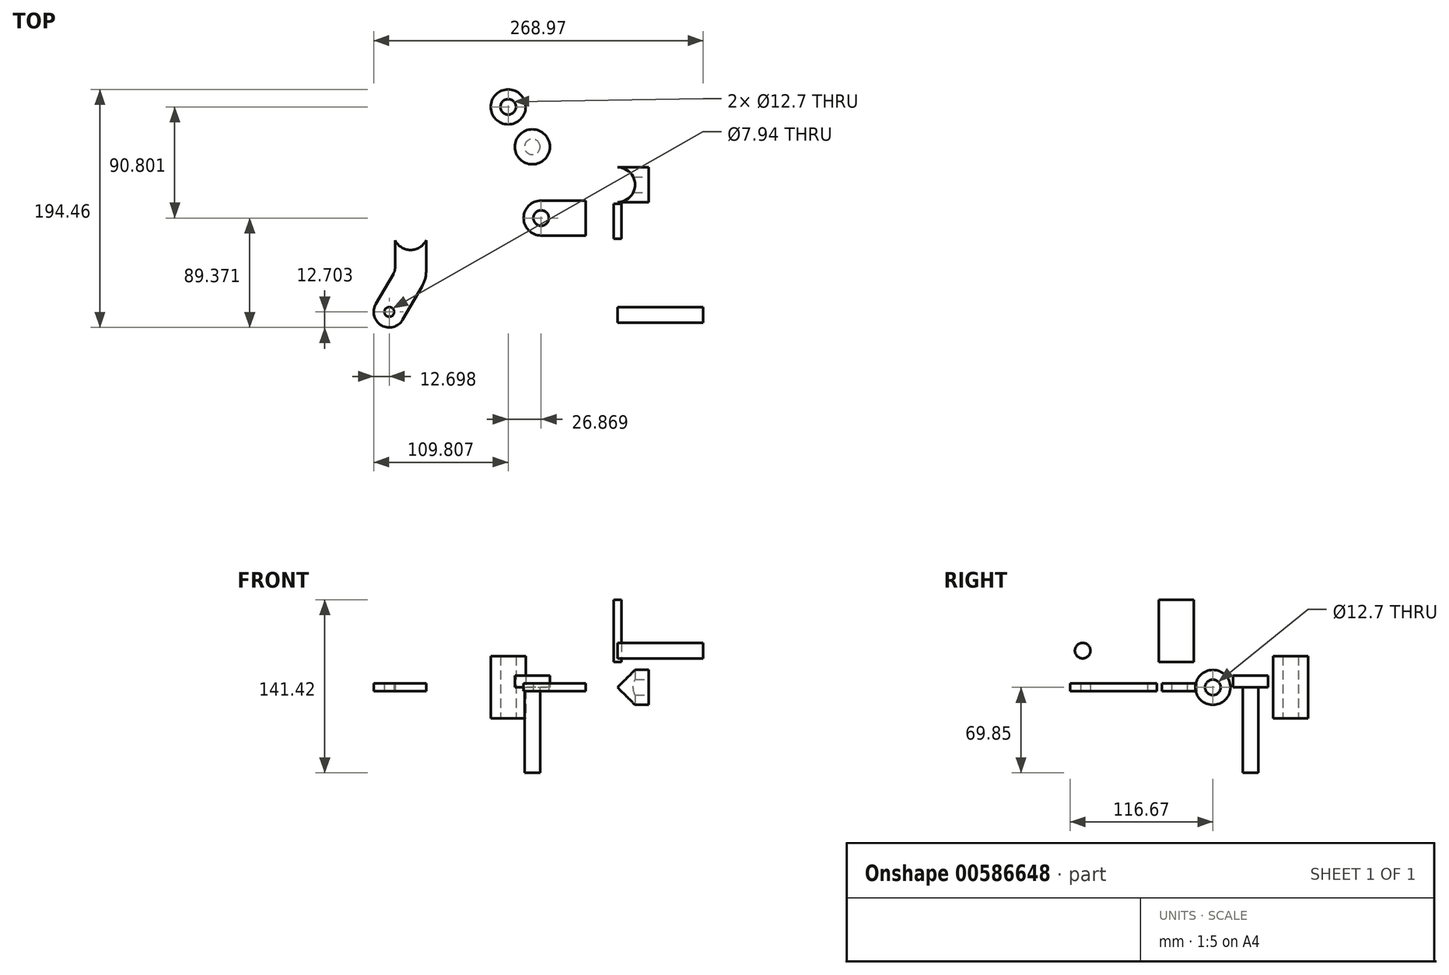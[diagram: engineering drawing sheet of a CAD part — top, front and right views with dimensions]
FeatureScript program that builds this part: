
annotation { "Feature Type Name" : "Feature", "Feature Type Description" : "" }
export const myFeature = defineFeature(function(context is Context, id is Id, definition is map)
    precondition{}
    {
        {
            var Q0;
            Q0=qCreatedBy(makeId("Top.planeOp"),FACE);
            var sketch = newSketch(context, id + "F0", { "sketchPlane" : qUnion([Q0])});
            skLineSegment(sketch, "E0.bottom", {"start": v(-76.73, -13.01) * mm, "end": v(-25.93, -13.01) * mm});
            skLineSegment(sketch, "E0.top", {"start": v(-76.73, -41.59) * mm, "end": v(-25.93, -41.59) * mm});
            skLineSegment(sketch, "E0.left", {"start": v(-76.73, -13.01) * mm, "end": v(-76.73, -41.59) * mm});
            skLineSegment(sketch, "E0.right", {"start": v(-25.93, -13.01) * mm, "end": v(-25.93, -41.59) * mm});
            skCircle(sketch, "E1", {"center": v(-62.44, -27.3) * mm, "radius": 6.35 * mm});
            skSolve(sketch);
        }
        {
            var Q0;
            Q0=makeQuery(id+"F0.imprint","IMPRINT",FACE,{"disambiguationData":[TD([[makeQuery(id+"F0.imprint","IMPRINT",EDGE,{"derivedFrom":sQuery(id+"F0.wireOp",EDGE,"E0.bottom")}),-1.0]])]});
            extrude(context, id + "F1", {"entities" : qUnion([Q0]), "depth" : 6.35 * mm, "offsetDistance" : 25.4 * mm, "symmetric" : true});
        }
        {
            var Q0;
            Q0=makeQuery(id+"F1.opExtrude","SWEPT_EDGE",EDGE,{"disambiguationData":[OSD([sQuery(id+"F0.wireOp",EDGE,"E0.bottom"),sQuery(id+"F0.wireOp",EDGE,"E0.left")])]});
            var Q1;
            Q1=makeQuery(id+"F1.opExtrude","SWEPT_EDGE",EDGE,{"disambiguationData":[OSD([sQuery(id+"F0.wireOp",EDGE,"E0.top"),sQuery(id+"F0.wireOp",EDGE,"E0.left")])]});
            fillet(context, id + "F2", {"entities" : qUnion([Q0, Q1]), "radius" : 14.29 * mm, "tangentPropagation" : true, "allowEdgeOverflow" : false});
        }
        {
            var Q0;
            Q0=qCreatedBy(makeId("Right.planeOp"),FACE);
            var sketch = newSketch(context, id + "F3", { "sketchPlane" : qUnion([Q0])});
            skLineSegment(sketch, "E2.bottom", {"start": v(-15.72, 71.57) * mm, "end": v(-44.3, 71.57) * mm});
            skLineSegment(sketch, "E2.top", {"start": v(-15.72, 20.77) * mm, "end": v(-44.3, 20.77) * mm});
            skLineSegment(sketch, "E2.left", {"start": v(-15.72, 71.57) * mm, "end": v(-15.72, 20.77) * mm});
            skLineSegment(sketch, "E2.right", {"start": v(-44.3, 71.57) * mm, "end": v(-44.3, 20.77) * mm});
            skSolve(sketch);
        }
        {
            var Q0;
            Q0=makeQuery(id+"F3.imprint","IMPRINT",FACE,{"disambiguationData":[TD([[makeQuery(id+"F3.imprint","IMPRINT",EDGE,{"derivedFrom":sQuery(id+"F3.wireOp",EDGE,"E2.bottom")}),1.0]])]});
            extrude(context, id + "F4", {"entities" : qUnion([Q0]), "depth" : 6.35 * mm, "offsetDistance" : 25.4 * mm, "symmetric" : true});
        }
        {
            var Q0;
            Q0=qCreatedBy(makeId("Top.planeOp"),FACE);
            var sketch = newSketch(context, id + "F5", { "sketchPlane" : qUnion([Q0])});
            skCircle(sketch, "E3", {"center": v(-89.31, 63.5) * mm, "radius": 14.29 * mm});
            skCircle(sketch, "E4", {"center": v(-89.31, 63.5) * mm, "radius": 6.35 * mm});
            skSolve(sketch);
        }
        {
            var Q0;
            Q0=makeQuery(id+"F5.imprint","IMPRINT",FACE,{"disambiguationData":[TD([[makeQuery(id+"F5.imprint","IMPRINT",EDGE,{"derivedFrom":sQuery(id+"F5.wireOp",EDGE,"E3")}),1.0]])]});
            extrude(context, id + "F6", {"entities" : qUnion([Q0]), "depth" : 50.8 * mm, "offsetDistance" : 25.4 * mm, "symmetric" : true});
        }
        {
            var Q0;
            Q0=qCreatedBy(makeId("Top.planeOp"),FACE);
            var sketch = newSketch(context, id + "F7", { "sketchPlane" : qUnion([Q0])});
            skCircle(sketch, "E5", {"center": v(-69.59, 30.87) * mm, "radius": 14.29 * mm});
            skSolve(sketch);
        }
        {
            var Q0;
            Q0=makeQuery(id+"F7.imprint","IMPRINT",FACE,{"disambiguationData":[TD([[makeQuery(id+"F7.imprint","IMPRINT",EDGE,{"derivedFrom":sQuery(id+"F7.wireOp",EDGE,"E5")}),1.0]])]});
            extrude(context, id + "F8", {"entities" : qUnion([Q0]), "depth" : 9.52 * mm, "offsetDistance" : 25.4 * mm});
        }
        {
            var Q0;
            Q0=makeQuery(id+"F8.opExtrude","CAP_FACE",FACE,{"disambiguationData":[OSD([sQuery(id+"F7.wireOp",EDGE,"E5")])],"isStart":true});
            var sketch = newSketch(context, id + "F9", { "sketchPlane" : qUnion([Q0])});
            skCircle(sketch, "E6", {"center": v(-69.59, -30.87) * mm, "radius": 6.35 * mm});
            skSolve(sketch);
        }
        {
            var Q0;
            Q0=makeQuery(id+"F9.imprint","IMPRINT",FACE,{"disambiguationData":[TD([[makeQuery(id+"F9.imprint","IMPRINT",EDGE,{"derivedFrom":sQuery(id+"F9.wireOp",EDGE,"E6")}),1.0]])]});
            extrude(context, id + "F10", {"entities" : qUnion([Q0]), "operationType" : NewBodyOperationType.ADD, "depth" : 69.85 * mm, "offsetDistance" : 25.4 * mm});
        }
        {
            var Q0;
            Q0=qCreatedBy(makeId("Right.planeOp"),FACE);
            var sketch = newSketch(context, id + "F11", { "sketchPlane" : qUnion([Q0])});
            skCircle(sketch, "E7", {"center": v(0, 0) * mm, "radius": 14.29 * mm});
            skSolve(sketch);
        }
        {
            var Q0;
            Q0=makeQuery(id+"F11.imprint","IMPRINT",FACE,{"disambiguationData":[TD([[makeQuery(id+"F11.imprint","IMPRINT",EDGE,{"derivedFrom":sQuery(id+"F11.wireOp",EDGE,"E7")}),1.0]])]});
            extrude(context, id + "F12", {"entities" : qUnion([Q0]), "depth" : 25.4 * mm, "offsetDistance" : 25.4 * mm});
        }
        {
            var Q0;
            Q0=makeQuery(id+"F12.opExtrude","CAP_FACE",FACE,{"disambiguationData":[OSD([sQuery(id+"F11.wireOp",EDGE,"E7")])],"isStart":false});
            var sketch = newSketch(context, id + "F13", { "sketchPlane" : qUnion([Q0])});
            skCircle(sketch, "E8", {"center": v(0, 0) * mm, "radius": 6.35 * mm});
            skSolve(sketch);
        }
        {
            var Q0;
            Q0=makeQuery(id+"F13.imprint","IMPRINT",FACE,{"disambiguationData":[TD([[makeQuery(id+"F13.imprint","IMPRINT",EDGE,{"derivedFrom":sQuery(id+"F13.wireOp",EDGE,"E8")}),1.0]])]});
            extrude(context, id + "F14", {"entities" : qUnion([Q0]), "operationType" : NewBodyOperationType.REMOVE, "oppositeDirection" : true, "depth" : 25.4 * mm, "offsetDistance" : 25.4 * mm});
        }
        {
            var Q0;
            Q0=qCreatedBy(makeId("Top.planeOp"),FACE);
            var sketch = newSketch(context, id + "F15", { "sketchPlane" : qUnion([Q0])});
            skCircle(sketch, "E9", {"center": v(0, 0) * mm, "radius": 14.29 * mm});
            skSolve(sketch);
        }
        {
            var Q0;
            Q0=makeQuery(id+"F15.imprint","IMPRINT",FACE,{"disambiguationData":[TD([[makeQuery(id+"F15.imprint","IMPRINT",EDGE,{"derivedFrom":sQuery(id+"F15.wireOp",EDGE,"E9")}),1.0]])]});
            extrude(context, id + "F16", {"entities" : qUnion([Q0]), "operationType" : NewBodyOperationType.REMOVE, "depth" : 28.57 * mm, "offsetDistance" : 25.4 * mm, "symmetric" : true});
        }
        {
            var Q0;
            Q0=qCreatedBy(makeId("Right.planeOp"),FACE);
            var sketch = newSketch(context, id + "F17", { "sketchPlane" : qUnion([Q0])});
            skCircle(sketch, "E10", {"center": v(-106.33, 30) * mm, "radius": 6.35 * mm});
            skSolve(sketch);
        }
        {
            var Q0;
            Q0=makeQuery(id+"F17.imprint","IMPRINT",FACE,{"disambiguationData":[TD([[makeQuery(id+"F17.imprint","IMPRINT",EDGE,{"derivedFrom":sQuery(id+"F17.wireOp",EDGE,"E10")}),1.0]])]});
            extrude(context, id + "F18", {"entities" : qUnion([Q0]), "depth" : 69.85 * mm, "offsetDistance" : 25.4 * mm});
        }
        {
            var Q0;
            Q0=qCreatedBy(makeId("Top.planeOp"),FACE);
            var sketch = newSketch(context, id + "F19", { "sketchPlane" : qUnion([Q0])});
            skLineSegment(sketch, "E11", {"start": v(-156.33, -45.62) * mm, "end": v(-156.33, -77.37) * mm});
            skLineSegment(sketch, "E12", {"start": v(-156.33, -77.37) * mm, "end": v(-175.43, -110.33) * mm});
            skLineSegment(sketch, "E13", {"start": v(-192.79, -114.96) * mm, "end": v(-192.79, -114.96) * mm});
            skLineSegment(sketch, "E14", {"start": v(-197.41, -97.6) * mm, "end": v(-181.73, -70.54) * mm});
            skLineSegment(sketch, "E15", {"start": v(-181.73, -70.54) * mm, "end": v(-181.73, -45.62) * mm});
            skArc(sketch, "E16", {"start": v(-181.73, -45.62) * mm, "mid": v(-169.03, -53.36) * mm, "end": v(-156.33, -45.62) * mm});
            skCircle(sketch, "E17", {"center": v(-186.42, -103.97) * mm, "radius": 3.97 * mm});
            skPoint(sketch, "E18.visualSharp", {"position": v(-203.78, -108.59) * mm});
            skArc(sketch, "E18.filletArc", {"start": v(-197.41, -97.6) * mm, "mid": v(-198.7, -107.24) * mm, "end": v(-192.79, -114.96) * mm});
            skPoint(sketch, "E19.visualSharp", {"position": v(-181.8, -121.32) * mm});
            skArc(sketch, "E19.filletArc", {"start": v(-192.79, -114.96) * mm, "mid": v(-183.15, -116.24) * mm, "end": v(-175.43, -110.33) * mm});
            skLineSegment(sketch, "E20", {"start": v(-186.42, -103.97) * mm, "end": v(-169.03, -39.07) * mm, "construction": true});
            skSolve(sketch);
        }
        {
            var Q0;
            Q0=makeQuery(id+"F19.imprint","IMPRINT",FACE,{"disambiguationData":[TD([[makeQuery(id+"F19.imprint","IMPRINT",EDGE,{"derivedFrom":sQuery(id+"F19.wireOp",EDGE,"E11")}),-1.0]])]});
            extrude(context, id + "F20", {"entities" : qUnion([Q0]), "depth" : 6.35 * mm, "offsetDistance" : 25.4 * mm, "symmetric" : true});
        }
        {
            var Q0;
            Q0=makeQuery(id+"F20.opExtrude","SWEPT_EDGE",EDGE,{"disambiguationData":[OSD([sQuery(id+"F19.wireOp",EDGE,"E14"),sQuery(id+"F19.wireOp",EDGE,"E15")])]});
            fillet(context, id + "F21", {"entities" : qUnion([Q0]), "radius" : 9.52 * mm, "tangentPropagation" : true, "allowEdgeOverflow" : false});
        }
        {
            var Q0;
            Q0=makeQuery(id+"F20.opExtrude","SWEPT_EDGE",EDGE,{"disambiguationData":[OSD([sQuery(id+"F19.wireOp",EDGE,"E11"),sQuery(id+"F19.wireOp",EDGE,"E12")])]});
            fillet(context, id + "F22", {"entities" : qUnion([Q0]), "radius" : 25.4 * mm, "tangentPropagation" : true, "allowEdgeOverflow" : false});
        }
    });
